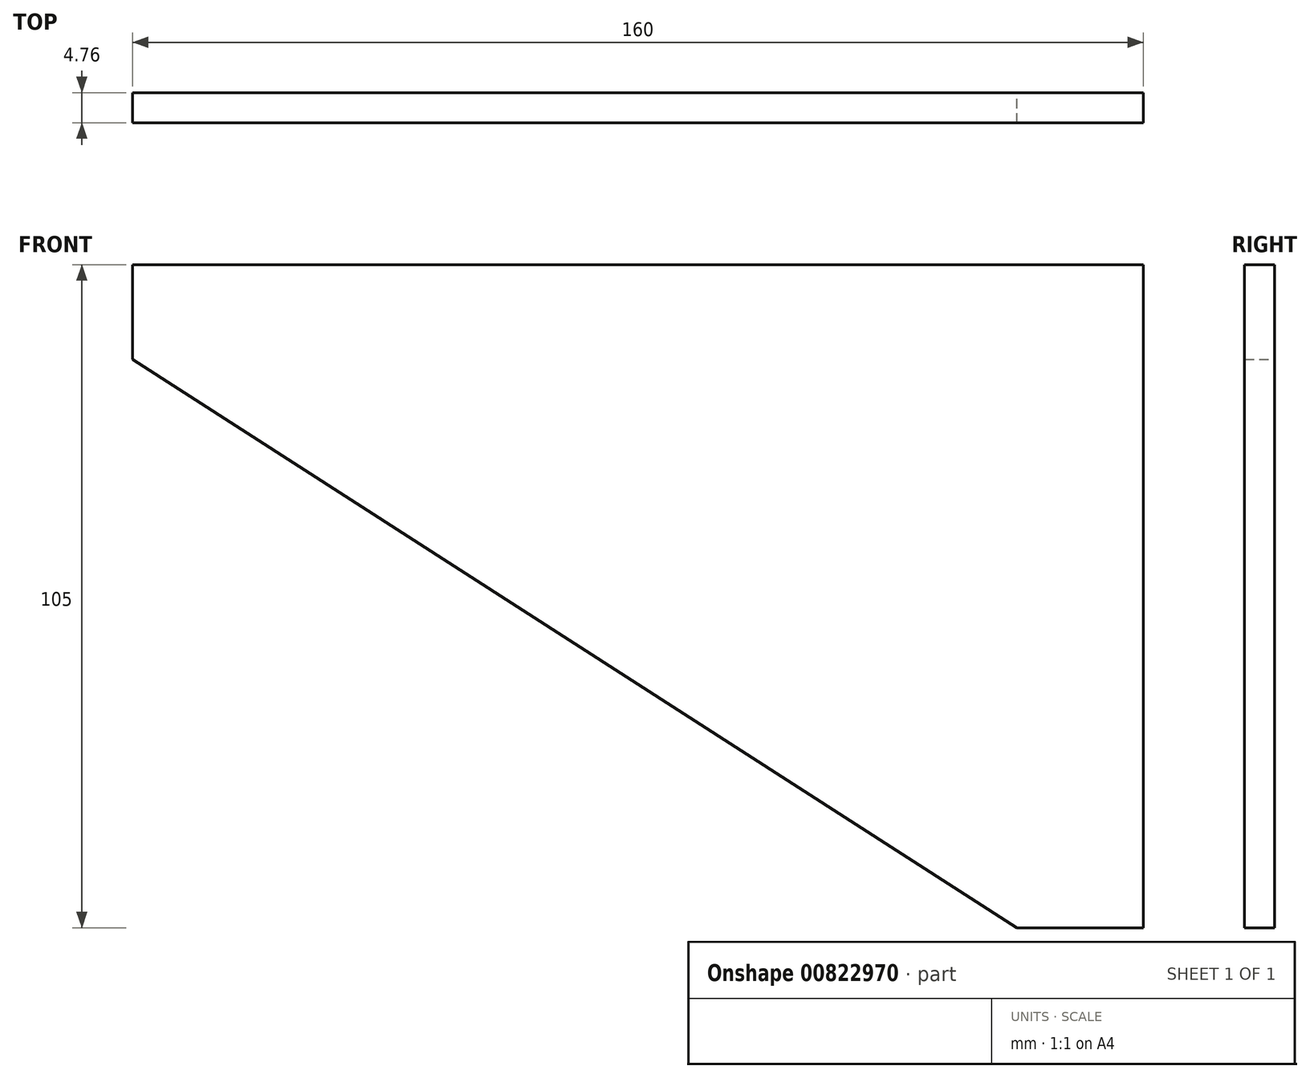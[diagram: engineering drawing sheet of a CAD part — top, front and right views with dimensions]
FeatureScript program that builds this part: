
annotation { "Feature Type Name" : "Feature", "Feature Type Description" : "" }
export const myFeature = defineFeature(function(context is Context, id is Id, definition is map)
    precondition{}
    {
        {
            var Q0;
            Q0=qCreatedBy(makeId("Front.planeOp"),FACE);
            var sketch = newSketch(context, id + "F0", { "sketchPlane" : qUnion([Q0])});
            skLineSegment(sketch, "E0", {"start": v(0, 0) * mm, "end": v(-160, 0) * mm});
            skLineSegment(sketch, "E1", {"start": v(-160, 0) * mm, "end": v(-160, -15) * mm});
            skLineSegment(sketch, "E2", {"start": v(-160, -15) * mm, "end": v(-20, -105) * mm});
            skLineSegment(sketch, "E3", {"start": v(-20, -105) * mm, "end": v(0, -105) * mm});
            skLineSegment(sketch, "E4", {"start": v(0, -105) * mm, "end": v(0, 0) * mm});
            skSolve(sketch);
        }
        {
            var Q0;
            Q0 = qSketchRegion(id + "F0", true);
            extrude(context, id + "F1", {"entities" : qUnion([Q0]), "endBound" : BoundingType.SYMMETRIC, "depth" : (3 * 25.4 / 16) * mm, "offsetDistance" : 25 * mm});
        }
    });
